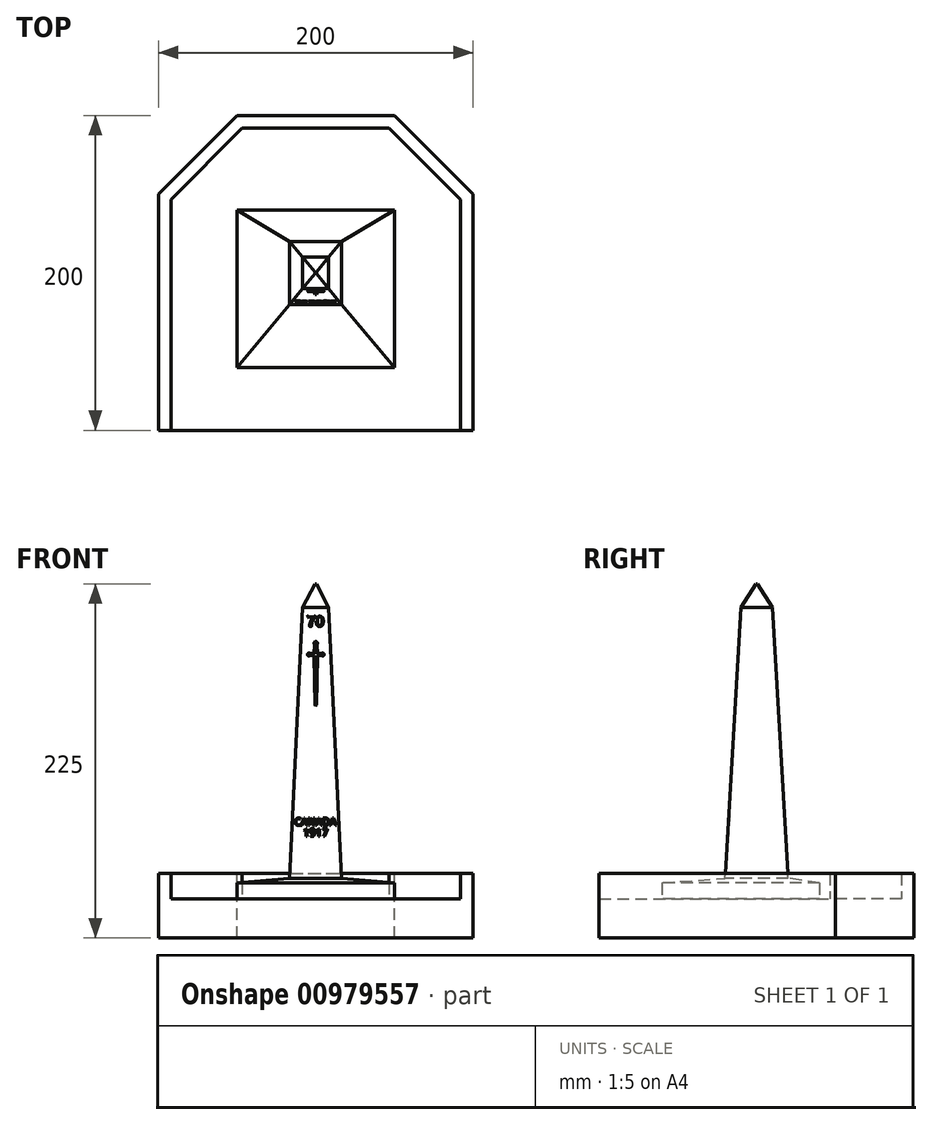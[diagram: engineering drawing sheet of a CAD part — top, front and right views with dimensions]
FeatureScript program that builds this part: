
annotation { "Feature Type Name" : "Feature", "Feature Type Description" : "" }
export const myFeature = defineFeature(function(context is Context, id is Id, definition is map)
    precondition{}
    {
        {
            var Q0;
            Q0=qCreatedBy(makeId("Top.planeOp"),FACE);
            cPlane(context, id + "F0", {"entities" : qUnion([Q0]), "cplaneType" : CPlaneType.OFFSET, "offset" : 13 * mm, "width" : 150 * mm, "height" : 150 * mm});
        }
        {
            var Q0;
            Q0=qCreatedBy(makeId("Top.planeOp"),FACE);
            cPlane(context, id + "F1", {"entities" : qUnion([Q0]), "cplaneType" : CPlaneType.OFFSET, "offset" : 185 * mm, "width" : 150 * mm, "height" : 150 * mm});
        }
        {
            var Q0;
            Q0=qCreatedBy(makeId("Top.planeOp"),FACE);
            cPlane(context, id + "F2", {"entities" : qUnion([Q0]), "cplaneType" : CPlaneType.OFFSET, "offset" : 200 * mm, "width" : 150 * mm, "height" : 150 * mm});
        }
        {
            var Q0;
            Q0=qCreatedBy(makeId("Top.planeOp"),FACE);
            var sketch = newSketch(context, id + "F3", { "sketchPlane" : qUnion([Q0])});
            skLineSegment(sketch, "E0.bottom", {"start": v(-50, 50) * mm, "end": v(50, 50) * mm});
            skLineSegment(sketch, "E0.top", {"start": v(-50, -50) * mm, "end": v(50, -50) * mm});
            skLineSegment(sketch, "E0.left", {"start": v(-50, 50) * mm, "end": v(-50, -50) * mm});
            skLineSegment(sketch, "E0.right", {"start": v(50, 50) * mm, "end": v(50, -50) * mm});
            skPoint(sketch, "E0.middle", {"position": v(0, 0) * mm});
            skSolve(sketch);
        }
        {
            var Q0;
            Q0=makeQuery(id+"F3.imprint","IMPRINT",FACE,{"disambiguationData":[TD([[makeQuery(id+"F3.imprint","IMPRINT",EDGE,{"derivedFrom":sQuery(id+"F3.wireOp",EDGE,"E0.bottom")}),-1.0]])]});
            extrude(context, id + "F4", {"entities" : qUnion([Q0]), "depth" : 10 * mm, "offsetDistance" : 25 * mm});
        }
        {
            var Q0;
            Q0=qCreatedBy(id+"F0.planeOp",FACE);
            var sketch = newSketch(context, id + "F5", { "sketchPlane" : qUnion([Q0])});
            skLineSegment(sketch, "E1.bottom", {"start": v(-16.5, 30) * mm, "end": v(16.5, 30) * mm});
            skLineSegment(sketch, "E1.top", {"start": v(-16.5, -10) * mm, "end": v(16.5, -10) * mm});
            skLineSegment(sketch, "E1.left", {"start": v(-16.5, 30) * mm, "end": v(-16.5, -10) * mm});
            skLineSegment(sketch, "E1.right", {"start": v(16.5, 30) * mm, "end": v(16.5, -10) * mm});
            skPoint(sketch, "E1.middle", {"position": v(0, 0) * mm});
            skSolve(sketch);
        }
        {
            var Q0;
            Q0=qCreatedBy(id+"F1.planeOp",FACE);
            var sketch = newSketch(context, id + "F6", { "sketchPlane" : qUnion([Q0])});
            skLineSegment(sketch, "E2.bottom", {"start": v(-8.25, 20) * mm, "end": v(8.25, 20) * mm});
            skLineSegment(sketch, "E2.top", {"start": v(-8.25, 0) * mm, "end": v(8.25, 0) * mm});
            skLineSegment(sketch, "E2.left", {"start": v(-8.25, 20) * mm, "end": v(-8.25, 0) * mm});
            skLineSegment(sketch, "E2.right", {"start": v(8.25, 20) * mm, "end": v(8.25, 0) * mm});
            skCircle(sketch, "E3", {"center": v(0, 10) * mm, "radius": 12.96 * mm, "construction": true});
            skSolve(sketch);
        }
        {
            var Q0;
            Q0=qCreatedBy(id+"F2.planeOp",FACE);
            var sketch = newSketch(context, id + "F7", { "sketchPlane" : qUnion([Q0])});
            skLineSegment(sketch, "E4.bottom", {"start": v(-0.4, 10.4) * mm, "end": v(0.4, 10.4) * mm});
            skLineSegment(sketch, "E4.top", {"start": v(-0.4, 9.6) * mm, "end": v(0.4, 9.6) * mm});
            skLineSegment(sketch, "E4.left", {"start": v(-0.4, 10.4) * mm, "end": v(-0.4, 9.6) * mm});
            skLineSegment(sketch, "E4.right", {"start": v(0.4, 10.4) * mm, "end": v(0.4, 9.6) * mm});
            skPoint(sketch, "E4.middle", {"position": v(0, 0) * mm});
            skSolve(sketch);
        }
        {
            var Q1;
            Q1=makeQuery(id+"F4.opExtrude","CAP_FACE",FACE,{"disambiguationData":[OSD([sQuery(id+"F3.wireOp",EDGE,"E0.bottom"),sQuery(id+"F3.wireOp",EDGE,"E0.top"),sQuery(id+"F3.wireOp",EDGE,"E0.left"),sQuery(id+"F3.wireOp",EDGE,"E0.right")])],"isStart":false});
            var Q2;
            Q2=makeQuery(id+"F5.imprint","IMPRINT",FACE,{"disambiguationData":[TD([[makeQuery(id+"F5.imprint","IMPRINT",EDGE,{"derivedFrom":sQuery(id+"F5.wireOp",EDGE,"E1.bottom")}),-1.0]])]});
            loft(context, id + "F8", {"operationType" : NewBodyOperationType.ADD, "sheetProfilesArray" : [{ "sheetProfileEntities" : qUnion([Q1]) }, { "sheetProfileEntities" : qUnion([Q2]) }]});
        }
        {
            var Q1;
            Q1=makeQuery(id+"F5.imprint","IMPRINT",FACE,{"disambiguationData":[TD([[makeQuery(id+"F5.imprint","IMPRINT",EDGE,{"derivedFrom":sQuery(id+"F5.wireOp",EDGE,"E1.bottom")}),-1.0]])]});
            var Q2;
            Q2=makeQuery(id+"F6.imprint","IMPRINT",FACE,{"disambiguationData":[TD([[makeQuery(id+"F6.imprint","IMPRINT",EDGE,{"derivedFrom":sQuery(id+"F6.wireOp",EDGE,"E2.bottom")}),-1.0]])]});
            loft(context, id + "F9", {"operationType" : NewBodyOperationType.ADD, "sheetProfilesArray" : [{ "sheetProfileEntities" : qUnion([Q1]) }, { "sheetProfileEntities" : qUnion([Q2]) }]});
        }
        {
            var Q1;
            Q1=makeQuery(id+"F9.opLoft","CAP_FACE",FACE,{"disambiguationData":[OSD([makeQuery(id+"F6.imprint","IMPRINT",FACE,{"disambiguationData":[TD([[makeQuery(id+"F6.imprint","IMPRINT",EDGE,{"derivedFrom":sQuery(id+"F6.wireOp",EDGE,"E2.bottom")}),-1.0]])]})])],"isStart":true});
            var Q2;
            Q2=makeQuery(id+"F7.imprint","IMPRINT",FACE,{"disambiguationData":[TD([[makeQuery(id+"F7.imprint","IMPRINT",EDGE,{"derivedFrom":sQuery(id+"F7.wireOp",EDGE,"E4.bottom")}),-1.0]])]});
            loft(context, id + "F10", {"operationType" : NewBodyOperationType.ADD, "sheetProfilesArray" : [{ "sheetProfileEntities" : qUnion([Q1]) }, { "sheetProfileEntities" : qUnion([Q2]) }]});
        }
        {
            var Q0;
            Q0=makeQuery(id+"F9.opLoft","SWEPT_FACE",FACE,{"disambiguationData":[OSD([sQuery(id+"F5.wireOp",EDGE,"E1.top"),sQuery(id+"F5.wireOp",EDGE,"E1.left"),sQuery(id+"F5.wireOp",EDGE,"E1.right"),sQuery(id+"F6.wireOp",EDGE,"E2.top"),sQuery(id+"F6.wireOp",EDGE,"E2.left"),sQuery(id+"F6.wireOp",EDGE,"E2.right")])]});
            var sketch = newSketch(context, id + "F11", { "sketchPlane" : qUnion([Q0])});
            skText(sketch, "E5", { "text": "70", "fontName": "Arimo-Regular.ttf"});
            const initialGuessF11  = {"E5": [-0.0055, 0.17263, 1, 0, 0.00693]};
            skSetInitialGuess(sketch, initialGuessF11);
            skSolve(sketch);
        }
        {
            var Q0;
            {var subQ0=sQuery(id+"F6.wireOp",EDGE,"E2.left");var subQ1=sQuery(id+"F6.wireOp",EDGE,"E2.top");var subQ3=sQuery(id+"F5.wireOp",EDGE,"E1.left");var subQ4=sQuery(id+"F5.wireOp",EDGE,"E1.top");var subQ6=sQuery(id+"F5.wireOp",EDGE,"E1.right");var subQ11=sQuery(id+"F6.wireOp",EDGE,"E2.right");Q0=makeQuery(id+"F13.boolean.opBoolean","SPLIT",FACE,{"disambiguationData":[TD([makeQuery(id+"F13.opExtrude","SWEPT_FACE",FACE,{"disambiguationData":[OSD([sQuery(id+"F11.wireOp",EDGE,"E5.sketch_text.stroke-0")])]})])],"derivedFrom":makeQuery(id+"F9.opLoft","SWEPT_FACE",FACE,{"disambiguationData":[OSD([subQ4,subQ3,subQ6,subQ1,subQ0,subQ11])]})});}
            var sketch = newSketch(context, id + "F12", { "sketchPlane" : qUnion([Q0])});
            skLineSegment(sketch, "E6", {"start": v(0, 122.1) * mm, "end": v(-0.4, 122.6) * mm});
            skLineSegment(sketch, "E7", {"start": v(-0.4, 122.6) * mm, "end": v(-1, 153.9) * mm});
            skLineSegment(sketch, "E8", {"start": v(-1, 153.9) * mm, "end": v(-3.74, 154.14) * mm});
            skLineSegment(sketch, "E9", {"start": v(0, 122.1) * mm, "end": v(0, 163.1) * mm, "construction": true});
            skCircle(sketch, "E10", {"center": v(-4.4, 154.75) * mm, "radius": 0.9 * mm});
            skPoint(sketch, "E10.second.point", {"position": v(-3.74, 155.36) * mm});
            skPoint(sketch, "E10.third.point", {"position": v(-5.3, 154.71) * mm});
            skLineSegment(sketch, "E11", {"start": v(-3.74, 155.36) * mm, "end": v(-1, 155.5) * mm});
            skLineSegment(sketch, "E12", {"start": v(-1, 155.5) * mm, "end": v(-0.66, 160.98) * mm});
            skArc(sketch, "E13", {"start": v(0, 163.1) * mm, "mid": v(-1.03, 162.26) * mm, "end": v(-0.66, 160.98) * mm});
            skArc(sketch, "E14.MirrorCS", {"start": v(0, 163.1) * mm, "mid": v(1.03, 162.26) * mm, "end": v(0.66, 160.98) * mm});
            skLineSegment(sketch, "E15.MirrorCS", {"start": v(1, 155.5) * mm, "end": v(0.66, 160.98) * mm});
            skLineSegment(sketch, "E16.MirrorCS", {"start": v(3.74, 155.36) * mm, "end": v(1, 155.5) * mm});
            skCircle(sketch, "E17.MirrorC", {"center": v(4.4, 154.75) * mm, "radius": 0.9 * mm});
            skLineSegment(sketch, "E18.MirrorCS", {"start": v(1, 153.9) * mm, "end": v(3.74, 154.14) * mm});
            skLineSegment(sketch, "E19.MirrorCS", {"start": v(0.4, 122.6) * mm, "end": v(1, 153.9) * mm});
            skLineSegment(sketch, "E20.MirrorCS", {"start": v(0, 122.1) * mm, "end": v(0.4, 122.6) * mm});
            skSolve(sketch);
        }
        {
            var Q0;
            Q0 = qSketchRegion(id + "F11", true);
            extrude(context, id + "F13", {"entities" : qUnion([Q0]), "operationType" : NewBodyOperationType.REMOVE, "oppositeDirection" : true, "depth" : .4 * mm, "offsetDistance" : 25 * mm});
        }
        {
            var Q0;
            Q0 = qSketchRegion(id + "F12", true);
            extrude(context, id + "F14", {"entities" : qUnion([Q0]), "operationType" : NewBodyOperationType.REMOVE, "oppositeDirection" : true, "depth" : .4 * mm, "offsetDistance" : 25 * mm});
        }
        {
            var Q0;
            Q0=makeQuery(id+"F13.boolean.opBoolean","COPY",EDGE,{"derivedFrom":makeQuery(id+"F13.opExtrude","CAP_EDGE",EDGE,{"disambiguationData":[OSD([sQuery(id+"F11.wireOp",EDGE,"E5.sketch_text.stroke-5")])],"isStart":true})});
            var Q1;
            Q1=makeQuery(id+"F13.boolean.opBoolean","COPY",EDGE,{"derivedFrom":makeQuery(id+"F13.opExtrude","CAP_EDGE",EDGE,{"disambiguationData":[OSD([sQuery(id+"F11.wireOp",EDGE,"E5.sketch_text.stroke-6")])],"isStart":true})});
            var Q2;
            Q2=makeQuery(id+"F13.boolean.opBoolean","COPY",EDGE,{"derivedFrom":makeQuery(id+"F13.opExtrude","CAP_EDGE",EDGE,{"disambiguationData":[OSD([sQuery(id+"F11.wireOp",EDGE,"E5.sketch_text.stroke-7")])],"isStart":true})});
            var Q3;
            Q3=makeQuery(id+"F13.boolean.opBoolean","COPY",EDGE,{"derivedFrom":makeQuery(id+"F13.opExtrude","CAP_EDGE",EDGE,{"disambiguationData":[OSD([sQuery(id+"F11.wireOp",EDGE,"E5.sketch_text.stroke-8")])],"isStart":true})});
            var Q4;
            Q4=makeQuery(id+"F13.boolean.opBoolean","COPY",EDGE,{"derivedFrom":makeQuery(id+"F13.opExtrude","CAP_EDGE",EDGE,{"disambiguationData":[OSD([sQuery(id+"F11.wireOp",EDGE,"E5.sketch_text.stroke-0")])],"isStart":true})});
            var Q5;
            Q5=makeQuery(id+"F13.boolean.opBoolean","COPY",EDGE,{"derivedFrom":makeQuery(id+"F13.opExtrude","CAP_EDGE",EDGE,{"disambiguationData":[OSD([sQuery(id+"F11.wireOp",EDGE,"E5.sketch_text.stroke-9")])],"isStart":true})});
            var Q6;
            Q6=makeQuery(id+"F13.boolean.opBoolean","COPY",EDGE,{"derivedFrom":makeQuery(id+"F13.opExtrude","CAP_EDGE",EDGE,{"disambiguationData":[OSD([sQuery(id+"F11.wireOp",EDGE,"E5.sketch_text.stroke-1")])],"isStart":true})});
            var Q7;
            Q7=makeQuery(id+"F13.boolean.opBoolean","COPY",EDGE,{"derivedFrom":makeQuery(id+"F13.opExtrude","CAP_EDGE",EDGE,{"disambiguationData":[OSD([sQuery(id+"F11.wireOp",EDGE,"E5.sketch_text.stroke-2")])],"isStart":true})});
            var Q8;
            Q8=makeQuery(id+"F13.boolean.opBoolean","COPY",EDGE,{"derivedFrom":makeQuery(id+"F13.opExtrude","CAP_EDGE",EDGE,{"disambiguationData":[OSD([sQuery(id+"F11.wireOp",EDGE,"E5.sketch_text.stroke-3")])],"isStart":true})});
            var Q9;
            Q9=makeQuery(id+"F13.boolean.opBoolean","COPY",EDGE,{"derivedFrom":makeQuery(id+"F13.opExtrude","CAP_EDGE",EDGE,{"disambiguationData":[OSD([sQuery(id+"F11.wireOp",EDGE,"E5.sketch_text.stroke-4")])],"isStart":true})});
            var Q10;
            Q10=makeQuery(id+"F13.boolean.opBoolean","COPY",EDGE,{"derivedFrom":makeQuery(id+"F13.opExtrude","CAP_EDGE",EDGE,{"disambiguationData":[OSD([sQuery(id+"F11.wireOp",EDGE,"E5.sketch_text.stroke-6")])],"isStart":false})});
            var Q11;
            Q11=makeQuery(id+"F13.boolean.opBoolean","COPY",EDGE,{"derivedFrom":makeQuery(id+"F13.opExtrude","CAP_EDGE",EDGE,{"disambiguationData":[OSD([sQuery(id+"F11.wireOp",EDGE,"E5.sketch_text.stroke-7")])],"isStart":false})});
            var Q12;
            Q12=makeQuery(id+"F13.boolean.opBoolean","COPY",EDGE,{"derivedFrom":makeQuery(id+"F13.opExtrude","CAP_EDGE",EDGE,{"disambiguationData":[OSD([sQuery(id+"F11.wireOp",EDGE,"E5.sketch_text.stroke-8")])],"isStart":false})});
            var Q13;
            Q13=makeQuery(id+"F13.boolean.opBoolean","COPY",EDGE,{"derivedFrom":makeQuery(id+"F13.opExtrude","CAP_EDGE",EDGE,{"disambiguationData":[OSD([sQuery(id+"F11.wireOp",EDGE,"E5.sketch_text.stroke-9")])],"isStart":false})});
            var Q14;
            Q14=makeQuery(id+"F13.boolean.opBoolean","COPY",EDGE,{"derivedFrom":makeQuery(id+"F13.opExtrude","CAP_EDGE",EDGE,{"disambiguationData":[OSD([sQuery(id+"F11.wireOp",EDGE,"E5.sketch_text.stroke-0")])],"isStart":false})});
            var Q15;
            Q15=makeQuery(id+"F13.boolean.opBoolean","COPY",EDGE,{"derivedFrom":makeQuery(id+"F13.opExtrude","CAP_EDGE",EDGE,{"disambiguationData":[OSD([sQuery(id+"F11.wireOp",EDGE,"E5.sketch_text.stroke-3")])],"isStart":false})});
            var Q16;
            Q16=makeQuery(id+"F13.boolean.opBoolean","COPY",EDGE,{"derivedFrom":makeQuery(id+"F13.opExtrude","CAP_EDGE",EDGE,{"disambiguationData":[OSD([sQuery(id+"F11.wireOp",EDGE,"E5.sketch_text.stroke-4")])],"isStart":false})});
            var Q17;
            Q17=makeQuery(id+"F13.boolean.opBoolean","COPY",EDGE,{"derivedFrom":makeQuery(id+"F13.opExtrude","CAP_EDGE",EDGE,{"disambiguationData":[OSD([sQuery(id+"F11.wireOp",EDGE,"E5.sketch_text.stroke-5")])],"isStart":false})});
            var Q18;
            Q18=makeQuery(id+"F13.boolean.opBoolean","COPY",EDGE,{"derivedFrom":makeQuery(id+"F13.opExtrude","CAP_EDGE",EDGE,{"disambiguationData":[OSD([sQuery(id+"F11.wireOp",EDGE,"E5.sketch_text.stroke-1")])],"isStart":false})});
            var Q19;
            Q19=makeQuery(id+"F13.boolean.opBoolean","COPY",EDGE,{"derivedFrom":makeQuery(id+"F13.opExtrude","CAP_EDGE",EDGE,{"disambiguationData":[OSD([sQuery(id+"F11.wireOp",EDGE,"E5.sketch_text.stroke-2")])],"isStart":false})});
            var Q20;
            Q20=makeQuery(id+"F13.boolean.opBoolean","COPY",EDGE,{"derivedFrom":makeQuery(id+"F13.opExtrude","CAP_EDGE",EDGE,{"disambiguationData":[OSD([sQuery(id+"F11.wireOp",EDGE,"E5.sketch_text.stroke-10")])],"isStart":false})});
            var Q21;
            Q21=makeQuery(id+"F13.boolean.opBoolean","COPY",EDGE,{"derivedFrom":makeQuery(id+"F13.opExtrude","CAP_EDGE",EDGE,{"disambiguationData":[OSD([sQuery(id+"F11.wireOp",EDGE,"E5.sketch_text.stroke-10")])],"isStart":true})});
            var Q22;
            Q22=makeQuery(id+"F13.boolean.opBoolean","COPY",EDGE,{"derivedFrom":makeQuery(id+"F13.opExtrude","CAP_EDGE",EDGE,{"disambiguationData":[OSD([sQuery(id+"F11.wireOp",EDGE,"E5.sketch_text.stroke-22")])],"isStart":false})});
            var Q23;
            Q23=makeQuery(id+"F13.boolean.opBoolean","COPY",EDGE,{"derivedFrom":makeQuery(id+"F13.opExtrude","CAP_EDGE",EDGE,{"disambiguationData":[OSD([sQuery(id+"F11.wireOp",EDGE,"E5.sketch_text.stroke-21")])],"isStart":true})});
            var Q24;
            Q24=makeQuery(id+"F13.boolean.opBoolean","COPY",EDGE,{"derivedFrom":makeQuery(id+"F13.opExtrude","CAP_EDGE",EDGE,{"disambiguationData":[OSD([sQuery(id+"F12.wireOp",EDGE,"E13")])],"isStart":false})});
            var Q25;
            Q25=makeQuery(id+"F13.boolean.opBoolean","COPY",EDGE,{"derivedFrom":makeQuery(id+"F13.opExtrude","CAP_EDGE",EDGE,{"disambiguationData":[OSD([sQuery(id+"F12.wireOp",EDGE,"E14.MirrorCS")])],"isStart":false})});
            var Q26;
            Q26=makeQuery(id+"F13.boolean.opBoolean","COPY",EDGE,{"derivedFrom":makeQuery(id+"F13.opExtrude","CAP_EDGE",EDGE,{"disambiguationData":[OSD([sQuery(id+"F12.wireOp",EDGE,"E14.MirrorCS")])],"isStart":true})});
            var Q27;
            Q27=makeQuery(id+"F13.boolean.opBoolean","COPY",EDGE,{"derivedFrom":makeQuery(id+"F13.opExtrude","CAP_EDGE",EDGE,{"disambiguationData":[OSD([sQuery(id+"F12.wireOp",EDGE,"E13")])],"isStart":true})});
            var Q28;
            Q28=makeQuery(id+"F13.boolean.opBoolean","COPY",EDGE,{"derivedFrom":makeQuery(id+"F13.opExtrude","CAP_EDGE",EDGE,{"disambiguationData":[OSD([sQuery(id+"F12.wireOp",EDGE,"E15.MirrorCS")])],"isStart":false})});
            var Q29;
            Q29=makeQuery(id+"F13.boolean.opBoolean","COPY",EDGE,{"derivedFrom":makeQuery(id+"F13.opExtrude","CAP_EDGE",EDGE,{"disambiguationData":[OSD([sQuery(id+"F12.wireOp",EDGE,"E15.MirrorCS")])],"isStart":true})});
            var Q30;
            Q30=makeQuery(id+"F13.boolean.opBoolean","COPY",EDGE,{"derivedFrom":makeQuery(id+"F13.opExtrude","CAP_EDGE",EDGE,{"disambiguationData":[OSD([sQuery(id+"F12.wireOp",EDGE,"E12")])],"isStart":false})});
            var Q31;
            Q31=makeQuery(id+"F13.boolean.opBoolean","COPY",EDGE,{"derivedFrom":makeQuery(id+"F13.opExtrude","CAP_EDGE",EDGE,{"disambiguationData":[OSD([sQuery(id+"F12.wireOp",EDGE,"E12")])],"isStart":true})});
            var Q32;
            Q32=makeQuery(id+"F13.boolean.opBoolean","COPY",EDGE,{"derivedFrom":makeQuery(id+"F13.opExtrude","CAP_EDGE",EDGE,{"disambiguationData":[OSD([sQuery(id+"F12.wireOp",EDGE,"E11")])],"isStart":false})});
            var Q33;
            Q33=makeQuery(id+"F13.boolean.opBoolean","COPY",EDGE,{"derivedFrom":makeQuery(id+"F13.opExtrude","CAP_EDGE",EDGE,{"disambiguationData":[OSD([sQuery(id+"F12.wireOp",EDGE,"E11")])],"isStart":true})});
            var Q34;
            Q34=makeQuery(id+"F13.boolean.opBoolean","COPY",EDGE,{"derivedFrom":makeQuery(id+"F13.opExtrude","CAP_EDGE",EDGE,{"disambiguationData":[OSD([sQuery(id+"F12.wireOp",EDGE,"E10")])],"isStart":false})});
            var Q35;
            Q35=makeQuery(id+"F13.boolean.opBoolean","COPY",EDGE,{"derivedFrom":makeQuery(id+"F13.opExtrude","CAP_EDGE",EDGE,{"disambiguationData":[OSD([sQuery(id+"F12.wireOp",EDGE,"E10")])],"isStart":true})});
            var Q36;
            Q36=makeQuery(id+"F13.boolean.opBoolean","COPY",EDGE,{"derivedFrom":makeQuery(id+"F13.opExtrude","CAP_EDGE",EDGE,{"disambiguationData":[OSD([sQuery(id+"F12.wireOp",EDGE,"E16.MirrorCS")])],"isStart":false})});
            var Q37;
            Q37=makeQuery(id+"F13.boolean.opBoolean","COPY",EDGE,{"derivedFrom":makeQuery(id+"F13.opExtrude","CAP_EDGE",EDGE,{"disambiguationData":[OSD([sQuery(id+"F12.wireOp",EDGE,"E16.MirrorCS")])],"isStart":true})});
            var Q38;
            Q38=makeQuery(id+"F13.boolean.opBoolean","COPY",EDGE,{"derivedFrom":makeQuery(id+"F13.opExtrude","CAP_EDGE",EDGE,{"disambiguationData":[OSD([sQuery(id+"F12.wireOp",EDGE,"E17.MirrorC")])],"isStart":false})});
            var Q39;
            Q39=makeQuery(id+"F13.boolean.opBoolean","COPY",EDGE,{"derivedFrom":makeQuery(id+"F13.opExtrude","CAP_EDGE",EDGE,{"disambiguationData":[OSD([sQuery(id+"F12.wireOp",EDGE,"E17.MirrorC")])],"isStart":true})});
            var Q40;
            Q40=makeQuery(id+"F13.boolean.opBoolean","COPY",EDGE,{"derivedFrom":makeQuery(id+"F13.opExtrude","CAP_EDGE",EDGE,{"disambiguationData":[OSD([sQuery(id+"F12.wireOp",EDGE,"E18.MirrorCS")])],"isStart":false})});
            var Q41;
            Q41=makeQuery(id+"F13.boolean.opBoolean","COPY",EDGE,{"derivedFrom":makeQuery(id+"F13.opExtrude","CAP_EDGE",EDGE,{"disambiguationData":[OSD([sQuery(id+"F12.wireOp",EDGE,"E18.MirrorCS")])],"isStart":true})});
            var Q42;
            Q42=makeQuery(id+"F13.boolean.opBoolean","COPY",EDGE,{"derivedFrom":makeQuery(id+"F13.opExtrude","CAP_EDGE",EDGE,{"disambiguationData":[OSD([sQuery(id+"F12.wireOp",EDGE,"E8")])],"isStart":false})});
            var Q43;
            Q43=makeQuery(id+"F13.boolean.opBoolean","COPY",EDGE,{"derivedFrom":makeQuery(id+"F13.opExtrude","CAP_EDGE",EDGE,{"disambiguationData":[OSD([sQuery(id+"F12.wireOp",EDGE,"E19.MirrorCS")])],"isStart":false})});
            var Q44;
            Q44=makeQuery(id+"F13.boolean.opBoolean","COPY",EDGE,{"derivedFrom":makeQuery(id+"F13.opExtrude","CAP_EDGE",EDGE,{"disambiguationData":[OSD([sQuery(id+"F12.wireOp",EDGE,"E19.MirrorCS")])],"isStart":true})});
            var Q45;
            Q45=makeQuery(id+"F13.boolean.opBoolean","COPY",EDGE,{"derivedFrom":makeQuery(id+"F13.opExtrude","CAP_EDGE",EDGE,{"disambiguationData":[OSD([sQuery(id+"F12.wireOp",EDGE,"E8")])],"isStart":true})});
            var Q46;
            Q46=makeQuery(id+"F13.boolean.opBoolean","COPY",EDGE,{"derivedFrom":makeQuery(id+"F13.opExtrude","CAP_EDGE",EDGE,{"disambiguationData":[OSD([sQuery(id+"F12.wireOp",EDGE,"E7")])],"isStart":false})});
            var Q47;
            Q47=makeQuery(id+"F13.boolean.opBoolean","COPY",EDGE,{"derivedFrom":makeQuery(id+"F13.opExtrude","CAP_EDGE",EDGE,{"disambiguationData":[OSD([sQuery(id+"F12.wireOp",EDGE,"E7")])],"isStart":true})});
            var Q48;
            Q48=makeQuery(id+"F13.boolean.opBoolean","COPY",EDGE,{"derivedFrom":makeQuery(id+"F13.opExtrude","CAP_EDGE",EDGE,{"disambiguationData":[OSD([sQuery(id+"F12.wireOp",EDGE,"E20.MirrorCS")])],"isStart":false})});
            var Q49;
            Q49=makeQuery(id+"F13.boolean.opBoolean","COPY",EDGE,{"derivedFrom":makeQuery(id+"F13.opExtrude","CAP_EDGE",EDGE,{"disambiguationData":[OSD([sQuery(id+"F12.wireOp",EDGE,"E20.MirrorCS")])],"isStart":true})});
            var Q50;
            Q50=makeQuery(id+"F13.boolean.opBoolean","COPY",EDGE,{"derivedFrom":makeQuery(id+"F13.opExtrude","CAP_EDGE",EDGE,{"disambiguationData":[OSD([sQuery(id+"F12.wireOp",EDGE,"E6")])],"isStart":true})});
            var Q51;
            Q51=makeQuery(id+"F13.boolean.opBoolean","COPY",EDGE,{"derivedFrom":makeQuery(id+"F13.opExtrude","CAP_EDGE",EDGE,{"disambiguationData":[OSD([sQuery(id+"F12.wireOp",EDGE,"E6")])],"isStart":false})});
            fillet(context, id + "F15", {"entities" : qUnion([Q0, Q1, Q2, Q3, Q4, Q5, Q6, Q7, Q8, Q9, Q10, Q11, Q12, Q13, Q14, Q15, Q16, Q17, Q18, Q19, Q20, Q21, Q22, Q23, Q24, Q25, Q26, Q27, Q28, Q29, Q30, Q31, Q32, Q33, Q34, Q35, Q36, Q37, Q38, Q39, Q40, Q41, Q42, Q43, Q44, Q45, Q46, Q47, Q48, Q49, Q50, Q51]), "radius" : .2 * mm, "tangentPropagation" : true, "allowEdgeOverflow" : false});
        }
        {
            var Q0;
            Q0=makeQuery(id+"F14.boolean.opBoolean","COPY",EDGE,{"derivedFrom":makeQuery(id+"F14.opExtrude","CAP_EDGE",EDGE,{"disambiguationData":[OSD([sQuery(id+"F12.wireOp",EDGE,"E14.MirrorCS")])],"isStart":false})});
            var Q1;
            Q1=makeQuery(id+"F14.boolean.opBoolean","COPY",EDGE,{"derivedFrom":makeQuery(id+"F14.opExtrude","CAP_EDGE",EDGE,{"disambiguationData":[OSD([sQuery(id+"F12.wireOp",EDGE,"E14.MirrorCS")])],"isStart":true})});
            var Q2;
            Q2=makeQuery(id+"F14.boolean.opBoolean","COPY",EDGE,{"derivedFrom":makeQuery(id+"F14.opExtrude","CAP_EDGE",EDGE,{"disambiguationData":[OSD([sQuery(id+"F12.wireOp",EDGE,"E13")])],"isStart":true})});
            var Q3;
            Q3=makeQuery(id+"F14.boolean.opBoolean","COPY",EDGE,{"derivedFrom":makeQuery(id+"F14.opExtrude","CAP_EDGE",EDGE,{"disambiguationData":[OSD([sQuery(id+"F12.wireOp",EDGE,"E13")])],"isStart":false})});
            var Q4;
            Q4=makeQuery(id+"F14.boolean.opBoolean","COPY",EDGE,{"derivedFrom":makeQuery(id+"F14.opExtrude","CAP_EDGE",EDGE,{"disambiguationData":[OSD([sQuery(id+"F12.wireOp",EDGE,"E12")])],"isStart":false})});
            var Q5;
            Q5=makeQuery(id+"F14.boolean.opBoolean","COPY",EDGE,{"derivedFrom":makeQuery(id+"F14.opExtrude","CAP_EDGE",EDGE,{"disambiguationData":[OSD([sQuery(id+"F12.wireOp",EDGE,"E12")])],"isStart":true})});
            var Q6;
            Q6=makeQuery(id+"F14.boolean.opBoolean","COPY",EDGE,{"derivedFrom":makeQuery(id+"F14.opExtrude","CAP_EDGE",EDGE,{"disambiguationData":[OSD([sQuery(id+"F12.wireOp",EDGE,"E15.MirrorCS")])],"isStart":false})});
            var Q7;
            Q7=makeQuery(id+"F14.boolean.opBoolean","COPY",EDGE,{"derivedFrom":makeQuery(id+"F14.opExtrude","CAP_EDGE",EDGE,{"disambiguationData":[OSD([sQuery(id+"F12.wireOp",EDGE,"E15.MirrorCS")])],"isStart":true})});
            var Q8;
            Q8=makeQuery(id+"F14.boolean.opBoolean","COPY",EDGE,{"derivedFrom":makeQuery(id+"F14.opExtrude","CAP_EDGE",EDGE,{"disambiguationData":[OSD([sQuery(id+"F12.wireOp",EDGE,"E16.MirrorCS")])],"isStart":false})});
            var Q9;
            Q9=makeQuery(id+"F14.boolean.opBoolean","COPY",EDGE,{"derivedFrom":makeQuery(id+"F14.opExtrude","CAP_EDGE",EDGE,{"disambiguationData":[OSD([sQuery(id+"F12.wireOp",EDGE,"E16.MirrorCS")])],"isStart":true})});
            var Q10;
            Q10=makeQuery(id+"F14.boolean.opBoolean","COPY",EDGE,{"derivedFrom":makeQuery(id+"F14.opExtrude","CAP_EDGE",EDGE,{"disambiguationData":[OSD([sQuery(id+"F12.wireOp",EDGE,"E17.MirrorC")])],"isStart":false})});
            var Q11;
            Q11=makeQuery(id+"F14.boolean.opBoolean","COPY",EDGE,{"derivedFrom":makeQuery(id+"F14.opExtrude","CAP_EDGE",EDGE,{"disambiguationData":[OSD([sQuery(id+"F12.wireOp",EDGE,"E17.MirrorC")])],"isStart":true})});
            var Q12;
            Q12=makeQuery(id+"F14.boolean.opBoolean","COPY",EDGE,{"derivedFrom":makeQuery(id+"F14.opExtrude","CAP_EDGE",EDGE,{"disambiguationData":[OSD([sQuery(id+"F12.wireOp",EDGE,"E18.MirrorCS")])],"isStart":true})});
            var Q13;
            Q13=makeQuery(id+"F14.boolean.opBoolean","COPY",EDGE,{"derivedFrom":makeQuery(id+"F14.opExtrude","CAP_EDGE",EDGE,{"disambiguationData":[OSD([sQuery(id+"F12.wireOp",EDGE,"E18.MirrorCS")])],"isStart":false})});
            var Q14;
            Q14=makeQuery(id+"F14.boolean.opBoolean","COPY",EDGE,{"derivedFrom":makeQuery(id+"F14.opExtrude","CAP_EDGE",EDGE,{"disambiguationData":[OSD([sQuery(id+"F12.wireOp",EDGE,"E8")])],"isStart":true})});
            var Q15;
            Q15=makeQuery(id+"F14.boolean.opBoolean","COPY",EDGE,{"derivedFrom":makeQuery(id+"F14.opExtrude","CAP_EDGE",EDGE,{"disambiguationData":[OSD([sQuery(id+"F12.wireOp",EDGE,"E8")])],"isStart":false})});
            var Q16;
            Q16=makeQuery(id+"F14.boolean.opBoolean","COPY",EDGE,{"derivedFrom":makeQuery(id+"F14.opExtrude","CAP_EDGE",EDGE,{"disambiguationData":[OSD([sQuery(id+"F12.wireOp",EDGE,"E10")])],"isStart":false})});
            var Q17;
            Q17=makeQuery(id+"F14.boolean.opBoolean","COPY",EDGE,{"derivedFrom":makeQuery(id+"F14.opExtrude","CAP_EDGE",EDGE,{"disambiguationData":[OSD([sQuery(id+"F12.wireOp",EDGE,"E10")])],"isStart":true})});
            var Q18;
            Q18=makeQuery(id+"F14.boolean.opBoolean","COPY",EDGE,{"derivedFrom":makeQuery(id+"F14.opExtrude","CAP_EDGE",EDGE,{"disambiguationData":[OSD([sQuery(id+"F12.wireOp",EDGE,"E11")])],"isStart":false})});
            var Q19;
            Q19=makeQuery(id+"F14.boolean.opBoolean","COPY",EDGE,{"derivedFrom":makeQuery(id+"F14.opExtrude","CAP_EDGE",EDGE,{"disambiguationData":[OSD([sQuery(id+"F12.wireOp",EDGE,"E11")])],"isStart":true})});
            var Q20;
            Q20=makeQuery(id+"F14.boolean.opBoolean","COPY",EDGE,{"derivedFrom":makeQuery(id+"F14.opExtrude","CAP_EDGE",EDGE,{"disambiguationData":[OSD([sQuery(id+"F12.wireOp",EDGE,"E19.MirrorCS")])],"isStart":false})});
            var Q21;
            Q21=makeQuery(id+"F14.boolean.opBoolean","COPY",EDGE,{"derivedFrom":makeQuery(id+"F14.opExtrude","CAP_EDGE",EDGE,{"disambiguationData":[OSD([sQuery(id+"F12.wireOp",EDGE,"E19.MirrorCS")])],"isStart":true})});
            var Q22;
            Q22=makeQuery(id+"F14.boolean.opBoolean","COPY",EDGE,{"derivedFrom":makeQuery(id+"F14.opExtrude","CAP_EDGE",EDGE,{"disambiguationData":[OSD([sQuery(id+"F12.wireOp",EDGE,"E7")])],"isStart":false})});
            var Q23;
            Q23=makeQuery(id+"F14.boolean.opBoolean","COPY",EDGE,{"derivedFrom":makeQuery(id+"F14.opExtrude","CAP_EDGE",EDGE,{"disambiguationData":[OSD([sQuery(id+"F12.wireOp",EDGE,"E7")])],"isStart":true})});
            var Q24;
            Q24=makeQuery(id+"F14.boolean.opBoolean","COPY",EDGE,{"derivedFrom":makeQuery(id+"F14.opExtrude","CAP_EDGE",EDGE,{"disambiguationData":[OSD([sQuery(id+"F12.wireOp",EDGE,"E6")])],"isStart":true})});
            var Q25;
            Q25=makeQuery(id+"F14.boolean.opBoolean","COPY",EDGE,{"derivedFrom":makeQuery(id+"F14.opExtrude","CAP_EDGE",EDGE,{"disambiguationData":[OSD([sQuery(id+"F12.wireOp",EDGE,"E6")])],"isStart":false})});
            var Q26;
            Q26=makeQuery(id+"F14.boolean.opBoolean","COPY",EDGE,{"derivedFrom":makeQuery(id+"F14.opExtrude","CAP_EDGE",EDGE,{"disambiguationData":[OSD([sQuery(id+"F12.wireOp",EDGE,"E20.MirrorCS")])],"isStart":false})});
            var Q27;
            Q27=makeQuery(id+"F14.boolean.opBoolean","COPY",EDGE,{"derivedFrom":makeQuery(id+"F14.opExtrude","CAP_EDGE",EDGE,{"disambiguationData":[OSD([sQuery(id+"F12.wireOp",EDGE,"E20.MirrorCS")])],"isStart":true})});
            fillet(context, id + "F16", {"entities" : qUnion([Q0, Q1, Q2, Q3, Q4, Q5, Q6, Q7, Q8, Q9, Q10, Q11, Q12, Q13, Q14, Q15, Q16, Q17, Q18, Q19, Q20, Q21, Q22, Q23, Q24, Q25, Q26, Q27]), "radius" : .2 * mm, "tangentPropagation" : true, "allowEdgeOverflow" : false});
        }
        {
            var Q0;
            Q0=makeQuery(id+"F4.opExtrude","CAP_FACE",FACE,{"disambiguationData":[OSD([sQuery(id+"F3.wireOp",EDGE,"E0.bottom"),sQuery(id+"F3.wireOp",EDGE,"E0.top"),sQuery(id+"F3.wireOp",EDGE,"E0.left"),sQuery(id+"F3.wireOp",EDGE,"E0.right")])],"isStart":true});
            var sketch = newSketch(context, id + "F17", { "sketchPlane" : qUnion([Q0])});
            skLineSegment(sketch, "E21", {"start": v(100, 90) * mm, "end": v(-100, 90) * mm});
            skLineSegment(sketch, "E22", {"start": v(-100, 90) * mm, "end": v(-100, -60) * mm});
            skLineSegment(sketch, "E23", {"start": v(-100, -60) * mm, "end": v(-50, -110) * mm});
            skLineSegment(sketch, "E24", {"start": v(-50, -110) * mm, "end": v(50, -110) * mm});
            skLineSegment(sketch, "E25", {"start": v(50, -110) * mm, "end": v(100, -60) * mm});
            skLineSegment(sketch, "E26", {"start": v(100, -60) * mm, "end": v(100, 90) * mm});
            skLineSegment(sketch, "E27.0", {"start": v(92, -56.69) * mm, "end": v(92, 90) * mm});
            skLineSegment(sketch, "E27.1", {"start": v(-92, 90) * mm, "end": v(-92, -56.69) * mm});
            skLineSegment(sketch, "E27.2", {"start": v(-92, -56.69) * mm, "end": v(-46.69, -102) * mm});
            skLineSegment(sketch, "E27.3", {"start": v(-46.69, -102) * mm, "end": v(46.69, -102) * mm});
            skLineSegment(sketch, "E27.4", {"start": v(46.69, -102) * mm, "end": v(92, -56.69) * mm});
            skSolve(sketch);
        }
        {
            var Q0;
            Q0 = qSketchRegion(id + "F17", true);
            extrude(context, id + "F18", {"entities" : qUnion([Q0]), "operationType" : NewBodyOperationType.ADD, "depth" : 25 * mm, "offsetDistance" : 25 * mm});
        }
        {
            var Q0;
            {var subQ4=sQuery(id+"F17.wireOp",EDGE,"E22");Q0=makeQuery(id+"F17.imprint","IMPRINT",FACE,{"disambiguationData":[TD([[makeQuery(id+"F17.imprint","IMPRINT",EDGE,{"derivedFrom":subQ4}),1.0]])]});}
            extrude(context, id + "F19", {"entities" : qUnion([Q0]), "operationType" : NewBodyOperationType.ADD, "oppositeDirection" : true, "depth" : 16 * mm, "offsetDistance" : 25 * mm});
        }
        {
            var Q0;
            {var subQ3=sQuery(id+"F6.wireOp",EDGE,"E2.right");var subQ4=sQuery(id+"F6.wireOp",EDGE,"E2.left");var subQ5=sQuery(id+"F6.wireOp",EDGE,"E2.top");var subQ8=sQuery(id+"F5.wireOp",EDGE,"E1.left");var subQ9=sQuery(id+"F5.wireOp",EDGE,"E1.top");var subQ11=sQuery(id+"F5.wireOp",EDGE,"E1.right");Q0=makeQuery(id+"F13.boolean.opBoolean","SPLIT",FACE,{"disambiguationData":[TD([makeQuery(id+"F13.opExtrude","SWEPT_FACE",FACE,{"disambiguationData":[OSD([sQuery(id+"F11.wireOp",EDGE,"E5.sketch_text.stroke-0")])]})])],"derivedFrom":makeQuery(id+"F9.opLoft","SWEPT_FACE",FACE,{"disambiguationData":[OSD([subQ9,subQ8,subQ11,subQ5,subQ4,subQ3])]})});}
            var sketch = newSketch(context, id + "F20", { "sketchPlane" : qUnion([Q0])});
            skText(sketch, "E28", { "text": "CANADA", "fontName": "OpenSans-Regular.ttf"});
            skText(sketch, "E29", { "text": "1917\n", "fontName": "OpenSans-Regular.ttf"});
            const initialGuessF20  = {"E28": [-0.0135, 0.04597, 1, 0, 0.00477], "E29": [-0.00799, 0.03897, 1, 0, 0.005]};
            skSetInitialGuess(sketch, initialGuessF20);
            skSolve(sketch);
        }
        {
            var Q0;
            Q0 = qSketchRegion(id + "F20", true);
            extrude(context, id + "F21", {"entities" : qUnion([Q0]), "operationType" : NewBodyOperationType.REMOVE, "oppositeDirection" : true, "depth" : .4 * mm, "offsetDistance" : 25 * mm});
        }
    });
